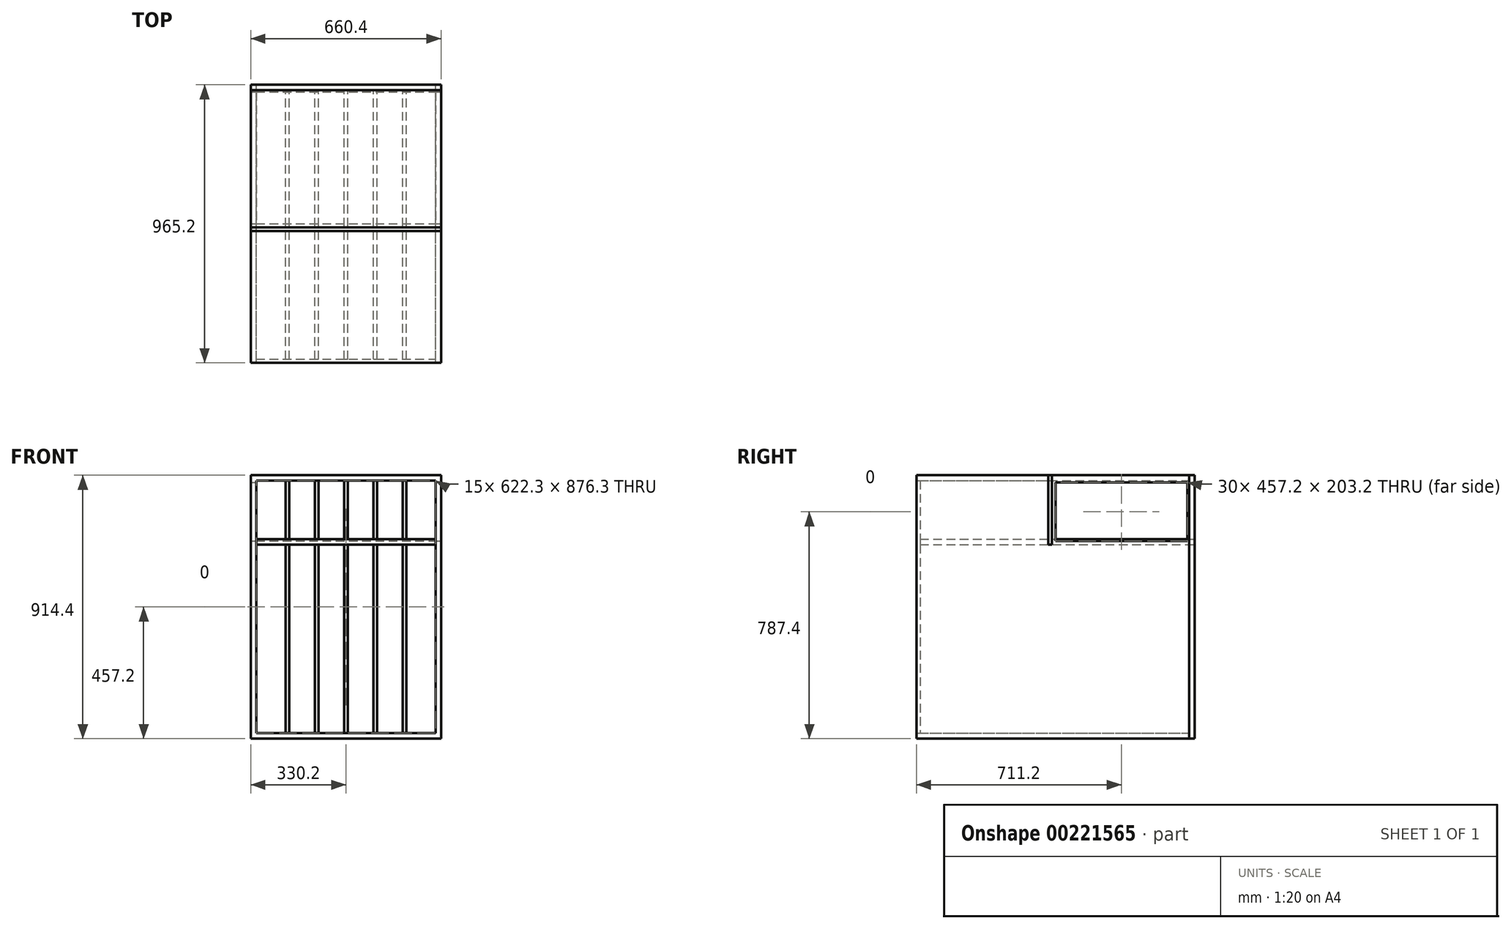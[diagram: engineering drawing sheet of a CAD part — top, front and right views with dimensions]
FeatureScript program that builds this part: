
annotation { "Feature Type Name" : "Feature", "Feature Type Description" : "" }
export const myFeature = defineFeature(function(context is Context, id is Id, definition is map)
    precondition{}
    {
        {
            var Q0;
            Q0=qCreatedBy(makeId("Front.planeOp"),FACE);
            var sketch = newSketch(context, id + "F0", { "sketchPlane" : qUnion([Q0])});
            skLineSegment(sketch, "E0.bottom", {"start": v(0, 0) * mm, "end": v(660.4, 0) * mm});
            skLineSegment(sketch, "E0.top", {"start": v(0, -914.4) * mm, "end": v(660.4, -914.4) * mm});
            skLineSegment(sketch, "E0.left", {"start": v(0, 0) * mm, "end": v(0, -914.4) * mm});
            skLineSegment(sketch, "E0.right", {"start": v(660.4, 0) * mm, "end": v(660.4, -914.4) * mm});
            skLineSegment(sketch, "E1.bottom", {"start": v(19.05, -19.05) * mm, "end": v(641.35, -19.05) * mm});
            skLineSegment(sketch, "E1.top", {"start": v(19.05, -895.35) * mm, "end": v(641.35, -895.35) * mm});
            skLineSegment(sketch, "E1.left", {"start": v(19.05, -19.05) * mm, "end": v(19.05, -895.35) * mm});
            skLineSegment(sketch, "E1.right", {"start": v(641.35, -19.05) * mm, "end": v(641.35, -895.35) * mm});
            skSolve(sketch);
        }
        {
            var Q0;
            Q0=makeQuery(id+"F0.imprint","IMPRINT",FACE,{"disambiguationData":[TD([[makeQuery(id+"F0.imprint","IMPRINT",EDGE,{"derivedFrom":sQuery(id+"F0.wireOp",EDGE,"E0.bottom")}),-1.0]])]});
            extrude(context, id + "F1", {"entities" : qUnion([Q0]), "depth" : 965.2 * mm});
        }
        {
            var Q0;
            Q0=qCreatedBy(makeId("Front.planeOp"),FACE);
            var sketch = newSketch(context, id + "F2", { "sketchPlane" : qUnion([Q0])});
            skLineSegment(sketch, "E2.bottom", {"start": v(0, 0) * mm, "end": v(660.4, 0) * mm});
            skLineSegment(sketch, "E2.top", {"start": v(0, -914.4) * mm, "end": v(660.4, -914.4) * mm});
            skLineSegment(sketch, "E2.left", {"start": v(0, 0) * mm, "end": v(0, -914.4) * mm});
            skLineSegment(sketch, "E2.right", {"start": v(660.4, 0) * mm, "end": v(660.4, -914.4) * mm});
            skSolve(sketch);
        }
        {
            var Q0;
            Q0=makeQuery(id+"F2.imprint","IMPRINT",FACE,{"disambiguationData":[TD([[makeQuery(id+"F2.imprint","IMPRINT",EDGE,{"derivedFrom":sQuery(id+"F2.wireOp",EDGE,"E2.bottom")}),-1.0]])]});
            extrude(context, id + "F3", {"entities" : qUnion([Q0]), "depth" : 19.05 * mm});
        }
        {
            var Q0;
            Q0=makeQuery(id+"F1.opExtrude","SWEPT_FACE",FACE,{"disambiguationData":[OSD([sQuery(id+"F0.wireOp",EDGE,"E0.right")])]});
            var sketch = newSketch(context, id + "F4", { "sketchPlane" : qUnion([Q0])});
            skLineSegment(sketch, "E3.bottom", {"start": v(-25.4, -25.4) * mm, "end": v(-482.6, -25.4) * mm});
            skLineSegment(sketch, "E3.top", {"start": v(-25.4, -228.6) * mm, "end": v(-482.6, -228.6) * mm});
            skLineSegment(sketch, "E3.left", {"start": v(-25.4, -25.4) * mm, "end": v(-25.4, -228.6) * mm});
            skLineSegment(sketch, "E3.right", {"start": v(-482.6, -25.4) * mm, "end": v(-482.6, -228.6) * mm});
            skSolve(sketch);
        }
        {
            var Q0;
            Q0=makeQuery(id+"F4.imprint","IMPRINT",FACE,{"disambiguationData":[TD([[makeQuery(id+"F4.imprint","IMPRINT",EDGE,{"derivedFrom":sQuery(id+"F4.wireOp",EDGE,"E3.bottom")}),1.0]])]});
            extrude(context, id + "F5", {"entities" : qUnion([Q0]), "operationType" : NewBodyOperationType.REMOVE, "oppositeDirection" : true, "depth" : 726.44 * mm});
        }
        {
            var Q0;
            Q0=qCreatedBy(makeId("Front.planeOp"),FACE);
            var sketch = newSketch(context, id + "F6", { "sketchPlane" : qUnion([Q0])});
            skLineSegment(sketch, "E4.bottom", {"start": v(19.05, -222.25) * mm, "end": v(641.35, -222.25) * mm});
            skLineSegment(sketch, "E4.top", {"start": v(19.05, -241.3) * mm, "end": v(641.35, -241.3) * mm});
            skLineSegment(sketch, "E4.left", {"start": v(19.05, -222.25) * mm, "end": v(19.05, -241.3) * mm});
            skLineSegment(sketch, "E4.right", {"start": v(641.35, -222.25) * mm, "end": v(641.35, -241.3) * mm});
            skSolve(sketch);
        }
        {
            var Q0;
            Q0=makeQuery(id+"F6.imprint","IMPRINT",FACE,{"disambiguationData":[TD([[makeQuery(id+"F6.imprint","IMPRINT",EDGE,{"derivedFrom":sQuery(id+"F6.wireOp",EDGE,"E4.bottom")}),-1.0]])]});
            extrude(context, id + "F7", {"entities" : qUnion([Q0]), "depth" : 952.5 * mm});
        }
        {
            var Q0;
            Q0=qCreatedBy(makeId("Right.planeOp"),FACE);
            var sketch = newSketch(context, id + "F8", { "sketchPlane" : qUnion([Q0])});
            skLineSegment(sketch, "E5.bottom", {"start": v(-495.3, 0) * mm, "end": v(-508, 0) * mm});
            skLineSegment(sketch, "E5.top", {"start": v(-495.3, -241.3) * mm, "end": v(-508, -241.3) * mm});
            skLineSegment(sketch, "E5.left", {"start": v(-495.3, 0) * mm, "end": v(-495.3, -241.3) * mm});
            skLineSegment(sketch, "E5.right", {"start": v(-508, 0) * mm, "end": v(-508, -241.3) * mm});
            skSolve(sketch);
        }
        {
            var Q0;
            Q0=makeQuery(id+"F8.imprint","IMPRINT",FACE,{"disambiguationData":[TD([[makeQuery(id+"F8.imprint","IMPRINT",EDGE,{"derivedFrom":sQuery(id+"F8.wireOp",EDGE,"E5.bottom")}),1.0]])]});
            extrude(context, id + "F9", {"entities" : qUnion([Q0]), "depth" : 660.4 * mm});
        }
        {
            var Q0;
            Q0=makeQuery(id+"F9.opExtrude","SWEPT_FACE",FACE,{"disambiguationData":[OSD([sQuery(id+"F8.wireOp",EDGE,"E5.right")])]});
            var sketch = newSketch(context, id + "F10", { "sketchPlane" : qUnion([Q0])});
            skLineSegment(sketch, "E6.bottom", {"start": v(120.65, -19.05) * mm, "end": v(133.35, -19.05) * mm});
            skLineSegment(sketch, "E6.top", {"start": v(120.65, -222.25) * mm, "end": v(133.35, -222.25) * mm});
            skLineSegment(sketch, "E6.left", {"start": v(120.65, -19.05) * mm, "end": v(120.65, -222.25) * mm});
            skLineSegment(sketch, "E6.right", {"start": v(133.35, -19.05) * mm, "end": v(133.35, -222.25) * mm});
            skLineSegment(sketch, "E7.1.0.0", {"start": v(222.25, -19.05) * mm, "end": v(222.25, -222.25) * mm});
            skLineSegment(sketch, "E7.1.0.1", {"start": v(234.95, -19.05) * mm, "end": v(234.95, -222.25) * mm});
            skLineSegment(sketch, "E7.1.0.2", {"start": v(222.25, -19.05) * mm, "end": v(234.95, -19.05) * mm});
            skLineSegment(sketch, "E7.1.0.3", {"start": v(222.25, -222.25) * mm, "end": v(234.95, -222.25) * mm});
            skLineSegment(sketch, "E7.2.0.0", {"start": v(323.85, -19.05) * mm, "end": v(323.85, -222.25) * mm});
            skLineSegment(sketch, "E7.2.0.1", {"start": v(336.55, -19.05) * mm, "end": v(336.55, -222.25) * mm});
            skLineSegment(sketch, "E7.2.0.2", {"start": v(323.85, -19.05) * mm, "end": v(336.55, -19.05) * mm});
            skLineSegment(sketch, "E7.2.0.3", {"start": v(323.85, -222.25) * mm, "end": v(336.55, -222.25) * mm});
            skLineSegment(sketch, "E7.3.0.0", {"start": v(425.45, -19.05) * mm, "end": v(425.45, -222.25) * mm});
            skLineSegment(sketch, "E7.3.0.1", {"start": v(438.15, -19.05) * mm, "end": v(438.15, -222.25) * mm});
            skLineSegment(sketch, "E7.3.0.2", {"start": v(425.45, -19.05) * mm, "end": v(438.15, -19.05) * mm});
            skLineSegment(sketch, "E7.3.0.3", {"start": v(425.45, -222.25) * mm, "end": v(438.15, -222.25) * mm});
            skLineSegment(sketch, "E7.4.0.0", {"start": v(527.05, -19.05) * mm, "end": v(527.05, -222.25) * mm});
            skLineSegment(sketch, "E7.4.0.1", {"start": v(539.75, -19.05) * mm, "end": v(539.75, -222.25) * mm});
            skLineSegment(sketch, "E7.4.0.2", {"start": v(527.05, -19.05) * mm, "end": v(539.75, -19.05) * mm});
            skLineSegment(sketch, "E7.4.0.3", {"start": v(527.05, -222.25) * mm, "end": v(539.75, -222.25) * mm});
            skLineSegment(sketch, "E7.direction1", {"start": v(120.65, -222.25) * mm, "end": v(222.25, -222.25) * mm, "construction": true});
            skSolve(sketch);
        }
        {
            var Q0;
            Q0=makeQuery(id+"F10.imprint","IMPRINT",FACE,{"disambiguationData":[TD([[makeQuery(id+"F10.imprint","IMPRINT",EDGE,{"derivedFrom":sQuery(id+"F10.wireOp",EDGE,"E6.bottom")}),-1.0]])]});
            var Q1;
            Q1=makeQuery(id+"F10.imprint","IMPRINT",FACE,{"disambiguationData":[TD([[makeQuery(id+"F10.imprint","IMPRINT",EDGE,{"derivedFrom":sQuery(id+"F10.wireOp",EDGE,"E7.1.0.0")}),1.0]])]});
            var Q2;
            Q2=makeQuery(id+"F10.imprint","IMPRINT",FACE,{"disambiguationData":[TD([[makeQuery(id+"F10.imprint","IMPRINT",EDGE,{"derivedFrom":sQuery(id+"F10.wireOp",EDGE,"E7.2.0.0")}),1.0]])]});
            var Q3;
            Q3=makeQuery(id+"F10.imprint","IMPRINT",FACE,{"disambiguationData":[TD([[makeQuery(id+"F10.imprint","IMPRINT",EDGE,{"derivedFrom":sQuery(id+"F10.wireOp",EDGE,"E7.3.0.0")}),1.0]])]});
            var Q4;
            Q4=makeQuery(id+"F10.imprint","IMPRINT",FACE,{"disambiguationData":[TD([[makeQuery(id+"F10.imprint","IMPRINT",EDGE,{"derivedFrom":sQuery(id+"F10.wireOp",EDGE,"E7.4.0.0")}),1.0]])]});
            extrude(context, id + "F11", {"entities" : qUnion([Q0, Q1, Q2, Q3, Q4]), "depth" : 444.5 * mm});
        }
        {
            var Q0;
            Q0=makeQuery(id+"F7.boolean.opBoolean","SPLIT",FACE,{"disambiguationData":[TD([makeQuery(id+"F1.opExtrude","SWEPT_FACE",FACE,{"disambiguationData":[OSD([sQuery(id+"F0.wireOp",EDGE,"E1.top")])]})])],"derivedFrom":makeQuery(id+"F3.opExtrude","CAP_FACE",FACE,{"disambiguationData":[OSD([sQuery(id+"F2.wireOp",EDGE,"E2.bottom"),sQuery(id+"F2.wireOp",EDGE,"E2.top"),sQuery(id+"F2.wireOp",EDGE,"E2.left"),sQuery(id+"F2.wireOp",EDGE,"E2.right")])],"isStart":false})});
            var sketch = newSketch(context, id + "F12", { "sketchPlane" : qUnion([Q0])});
            skLineSegment(sketch, "E8.bottom", {"start": v(120.65, -241.3) * mm, "end": v(133.35, -241.3) * mm});
            skLineSegment(sketch, "E8.top", {"start": v(120.65, -895.35) * mm, "end": v(133.35, -895.35) * mm});
            skLineSegment(sketch, "E8.left", {"start": v(120.65, -241.3) * mm, "end": v(120.65, -895.35) * mm});
            skLineSegment(sketch, "E8.right", {"start": v(133.35, -241.3) * mm, "end": v(133.35, -895.35) * mm});
            skLineSegment(sketch, "E9.1.0.0", {"start": v(234.95, -241.3) * mm, "end": v(234.95, -895.35) * mm});
            skLineSegment(sketch, "E9.1.0.1", {"start": v(222.25, -241.3) * mm, "end": v(222.25, -895.35) * mm});
            skLineSegment(sketch, "E9.1.0.2", {"start": v(222.25, -241.3) * mm, "end": v(234.95, -241.3) * mm});
            skLineSegment(sketch, "E9.1.0.3", {"start": v(222.25, -895.35) * mm, "end": v(234.95, -895.35) * mm});
            skLineSegment(sketch, "E9.2.0.0", {"start": v(336.55, -241.3) * mm, "end": v(336.55, -895.35) * mm});
            skLineSegment(sketch, "E9.2.0.1", {"start": v(323.85, -241.3) * mm, "end": v(323.85, -895.35) * mm});
            skLineSegment(sketch, "E9.2.0.2", {"start": v(323.85, -241.3) * mm, "end": v(336.55, -241.3) * mm});
            skLineSegment(sketch, "E9.2.0.3", {"start": v(323.85, -895.35) * mm, "end": v(336.55, -895.35) * mm});
            skLineSegment(sketch, "E9.3.0.0", {"start": v(438.15, -241.3) * mm, "end": v(438.15, -895.35) * mm});
            skLineSegment(sketch, "E9.3.0.1", {"start": v(425.45, -241.3) * mm, "end": v(425.45, -895.35) * mm});
            skLineSegment(sketch, "E9.3.0.2", {"start": v(425.45, -241.3) * mm, "end": v(438.15, -241.3) * mm});
            skLineSegment(sketch, "E9.3.0.3", {"start": v(425.45, -895.35) * mm, "end": v(438.15, -895.35) * mm});
            skLineSegment(sketch, "E9.4.0.0", {"start": v(539.75, -241.3) * mm, "end": v(539.75, -895.35) * mm});
            skLineSegment(sketch, "E9.4.0.1", {"start": v(527.05, -241.3) * mm, "end": v(527.05, -895.35) * mm});
            skLineSegment(sketch, "E9.4.0.2", {"start": v(527.05, -241.3) * mm, "end": v(539.75, -241.3) * mm});
            skLineSegment(sketch, "E9.4.0.3", {"start": v(527.05, -895.35) * mm, "end": v(539.75, -895.35) * mm});
            skLineSegment(sketch, "E9.direction1", {"start": v(120.65, -895.35) * mm, "end": v(222.25, -895.35) * mm, "construction": true});
            skSolve(sketch);
        }
        {
            var Q0;
            Q0=makeQuery(id+"F12.imprint","IMPRINT",FACE,{"disambiguationData":[TD([[makeQuery(id+"F12.imprint","IMPRINT",EDGE,{"derivedFrom":sQuery(id+"F12.wireOp",EDGE,"E9.1.0.0")}),-1.0]])]});
            var Q1;
            Q1=makeQuery(id+"F12.imprint","IMPRINT",FACE,{"disambiguationData":[TD([[makeQuery(id+"F12.imprint","IMPRINT",EDGE,{"derivedFrom":sQuery(id+"F12.wireOp",EDGE,"E9.2.0.0")}),-1.0]])]});
            var Q2;
            Q2=makeQuery(id+"F12.imprint","IMPRINT",FACE,{"disambiguationData":[TD([[makeQuery(id+"F12.imprint","IMPRINT",EDGE,{"derivedFrom":sQuery(id+"F12.wireOp",EDGE,"E9.3.0.0")}),-1.0]])]});
            var Q3;
            Q3=makeQuery(id+"F12.imprint","IMPRINT",FACE,{"disambiguationData":[TD([[makeQuery(id+"F12.imprint","IMPRINT",EDGE,{"derivedFrom":sQuery(id+"F12.wireOp",EDGE,"E9.4.0.0")}),-1.0]])]});
            var Q4;
            Q4=makeQuery(id+"F12.imprint","IMPRINT",FACE,{"disambiguationData":[TD([[makeQuery(id+"F12.imprint","IMPRINT",EDGE,{"derivedFrom":sQuery(id+"F12.wireOp",EDGE,"E8.bottom")}),-1.0]])]});
            extrude(context, id + "F13", {"entities" : qUnion([Q0, Q1, Q2, Q3, Q4]), "depth" : 933.45 * mm});
        }
    });
